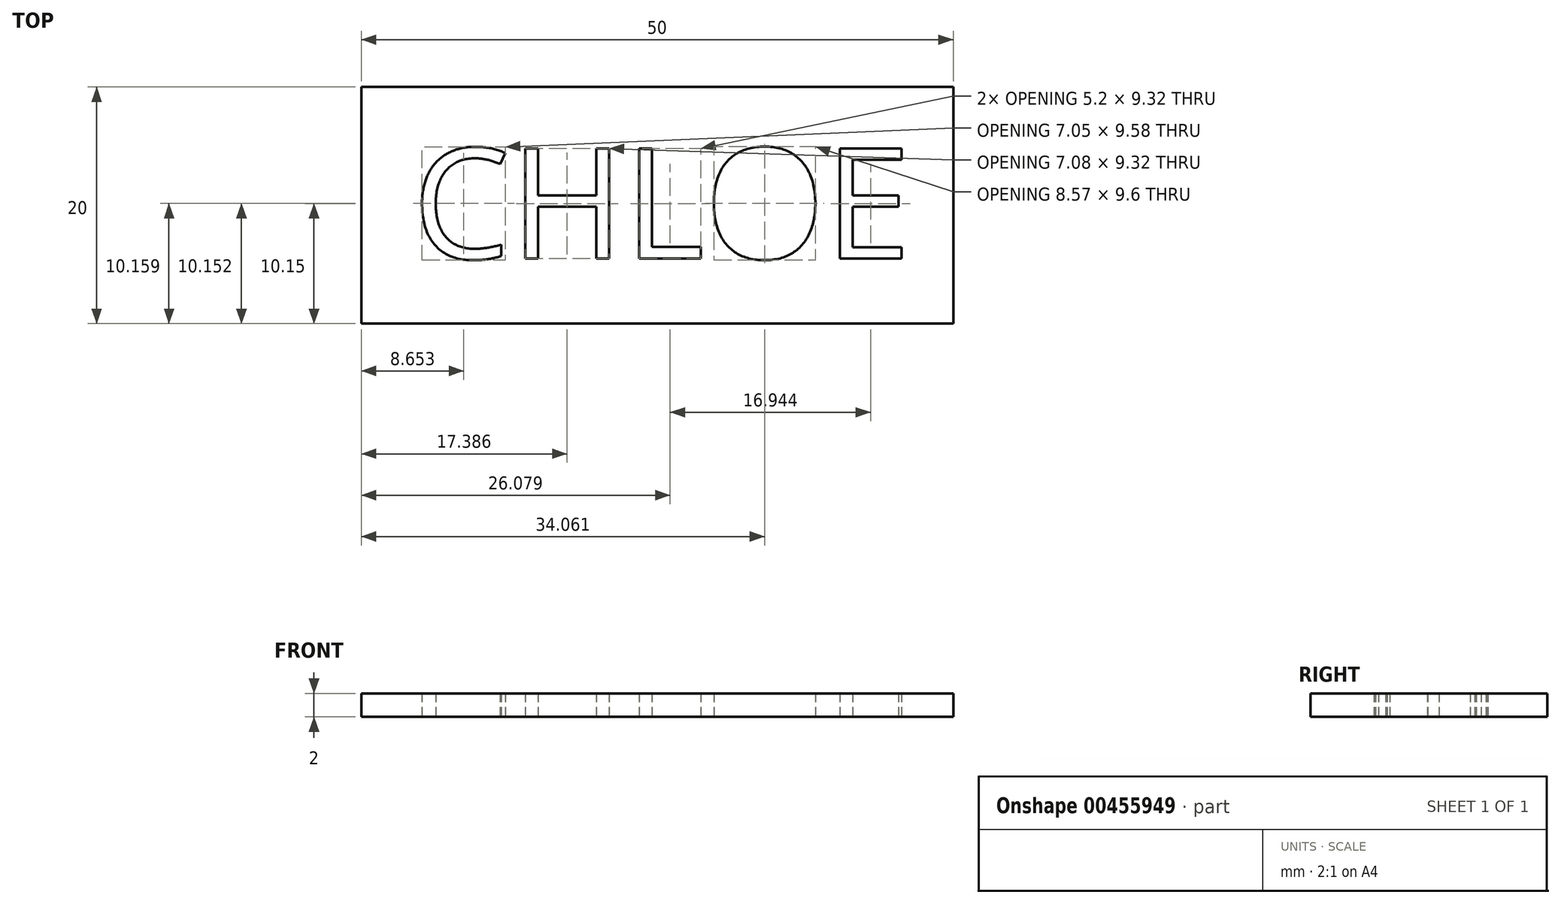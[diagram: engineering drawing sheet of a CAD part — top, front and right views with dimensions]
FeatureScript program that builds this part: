
annotation { "Feature Type Name" : "Feature", "Feature Type Description" : "" }
export const myFeature = defineFeature(function(context is Context, id is Id, definition is map)
    precondition{}
    {
        {
            var Q0;
            Q0=qCreatedBy(makeId("Top.planeOp"),FACE);
            var sketch = newSketch(context, id + "F0", { "sketchPlane" : qUnion([Q0])});
            skLineSegment(sketch, "E0.bottom", {"start": v(-25, 10) * mm, "end": v(25, 10) * mm});
            skLineSegment(sketch, "E0.top", {"start": v(-25, -10) * mm, "end": v(25, -10) * mm});
            skLineSegment(sketch, "E0.left", {"start": v(-25, 10) * mm, "end": v(-25, -10) * mm});
            skLineSegment(sketch, "E0.right", {"start": v(25, 10) * mm, "end": v(25, -10) * mm});
            skPoint(sketch, "E0.middle", {"position": v(0, 0) * mm});
            skText(sketch, "E1", { "text": "CHLOE", "fontName": "OpenSans-Regular.ttf"});
            const initialGuessF0  = {"E1": [-0.02067, -0.00451, 1, 0, 0.0094]};
            skSetInitialGuess(sketch, initialGuessF0);
            skSolve(sketch);
        }
        {
            var Q0;
            Q0=makeQuery(id+"F0.imprint","IMPRINT",FACE,{"disambiguationData":[TD([[makeQuery(id+"F0.imprint","IMPRINT",EDGE,{"derivedFrom":sQuery(id+"F0.wireOp",EDGE,"E0.bottom")}),-1.0]])]});
            extrude(context, id + "F1", {"entities" : qUnion([Q0]), "depth" : 2 * mm});
        }
    });
